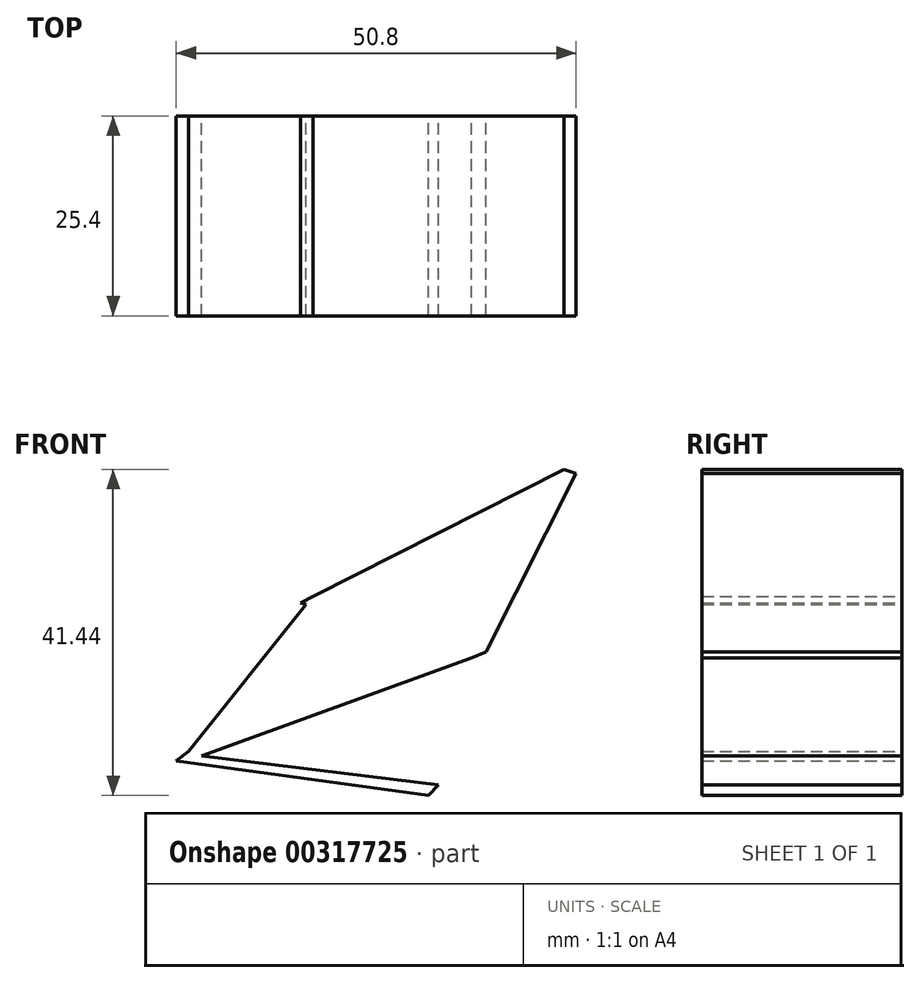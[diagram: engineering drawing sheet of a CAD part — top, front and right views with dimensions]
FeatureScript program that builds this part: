
annotation { "Feature Type Name" : "Feature", "Feature Type Description" : "" }
export const myFeature = defineFeature(function(context is Context, id is Id, definition is map)
    precondition{}
    {
        {
            var Q0;
            Q0=qCreatedBy(makeId("Front.planeOp"),FACE);
            var sketch = newSketch(context, id + "F0", { "sketchPlane" : qUnion([Q0])});
            skLineSegment(sketch, "E0", {"start": v(-57.8, -29.6) * mm, "end": v(-35.83, -36.67) * mm});
            skLineSegment(sketch, "E1", {"start": v(-35.83, -36.67) * mm, "end": v(-37.64, -37.44) * mm});
            skLineSegment(sketch, "E2", {"start": v(-37.64, -37.44) * mm, "end": v(-59.37, -30.4) * mm});
            skLineSegment(sketch, "E3", {"start": v(-57.8, -29.6) * mm, "end": v(-59.37, -30.4) * mm});
            skLineSegment(sketch, "E4", {"start": v(-57.8, -29.6) * mm, "end": v(-73.61, -49.31) * mm});
            skLineSegment(sketch, "E5", {"start": v(-73.61, -49.31) * mm, "end": v(-71.97, -49.84) * mm});
            skLineSegment(sketch, "E6", {"start": v(-71.97, -49.84) * mm, "end": v(-55.38, -31.7) * mm});
            skLineSegment(sketch, "E7", {"start": v(-55.38, -31.7) * mm, "end": v(-24.37, -13.95) * mm});
            skLineSegment(sketch, "E8", {"start": v(-24.37, -13.95) * mm, "end": v(-25.9, -13.46) * mm});
            skLineSegment(sketch, "E9", {"start": v(-25.9, -13.46) * mm, "end": v(-57.8, -29.6) * mm});
            skLineSegment(sketch, "E10", {"start": v(-24.37, -13.95) * mm, "end": v(-35.83, -36.67) * mm});
            skLineSegment(sketch, "E11", {"start": v(-71.97, -49.84) * mm, "end": v(-37.64, -37.44) * mm});
            skLineSegment(sketch, "E12", {"start": v(-71.97, -49.84) * mm, "end": v(-41.87, -53.52) * mm});
            skLineSegment(sketch, "E13", {"start": v(-41.87, -53.52) * mm, "end": v(-43.13, -54.9) * mm});
            skLineSegment(sketch, "E14", {"start": v(-43.13, -54.9) * mm, "end": v(-75.17, -50.48) * mm});
            skLineSegment(sketch, "E15", {"start": v(-75.17, -50.48) * mm, "end": v(-73.61, -49.31) * mm});
            skSolve(sketch);
        }
        {
            var Q0;
            Q0 = qSketchRegion(id + "F0", true);
            extrude(context, id + "F1", {"entities" : qUnion([Q0]), "depth" : 25.4 * mm});
        }
    });
